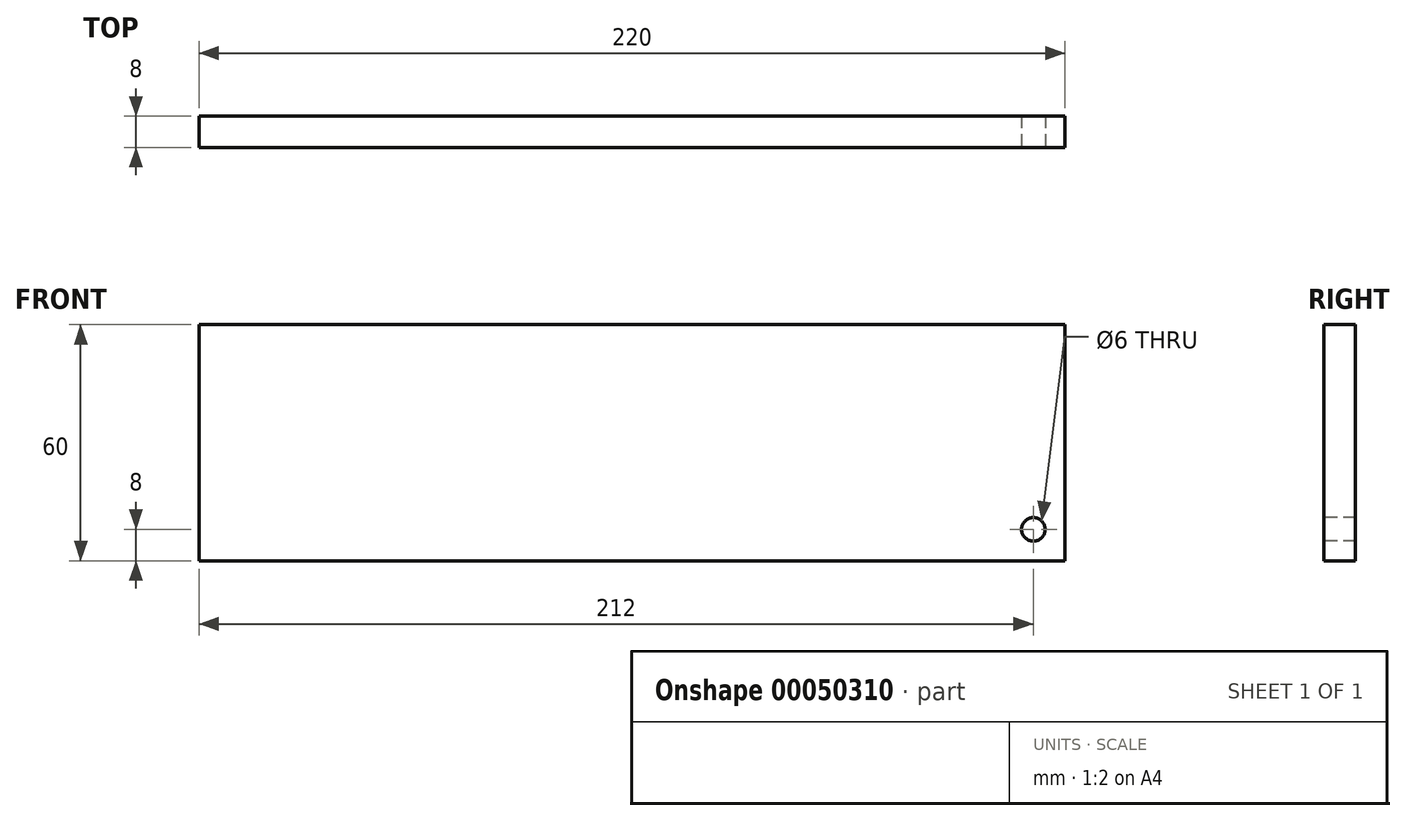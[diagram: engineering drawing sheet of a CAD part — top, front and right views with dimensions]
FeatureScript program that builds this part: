
annotation { "Feature Type Name" : "Feature", "Feature Type Description" : "" }
export const myFeature = defineFeature(function(context is Context, id is Id, definition is map)
    precondition{}
    {
        {
            var Q0;
            Q0=qCreatedBy(makeId("Front.planeOp"),FACE);
            var sketch = newSketch(context, id + "F0", { "sketchPlane" : qUnion([Q0])});
            skLineSegment(sketch, "E0.bottom", {"start": v(0, 0) * mm, "end": v(-220, 0) * mm});
            skLineSegment(sketch, "E0.top", {"start": v(0, -60) * mm, "end": v(-220, -60) * mm});
            skLineSegment(sketch, "E0.left", {"start": v(0, 0) * mm, "end": v(0, -60) * mm});
            skLineSegment(sketch, "E0.right", {"start": v(-220, 0) * mm, "end": v(-220, -60) * mm});
            skSolve(sketch);
        }
        {
            var Q0;
            Q0 = qSketchRegion(id + "F0", true);
            extrude(context, id + "F1", {"entities" : qUnion([Q0]), "depth" : 8 * mm});
        }
        {
            var Q0;
            Q0=makeQuery(id+"F1.opExtrude","CAP_FACE",FACE,{"disambiguationData":[OSD([sQuery(id+"F0.wireOp",EDGE,"E0.bottom"),sQuery(id+"F0.wireOp",EDGE,"E0.top"),sQuery(id+"F0.wireOp",EDGE,"E0.left"),sQuery(id+"F0.wireOp",EDGE,"E0.right")])],"isStart":false});
            var sketch = newSketch(context, id + "F2", { "sketchPlane" : qUnion([Q0])});
            skPoint(sketch, "E1", {"position": v(-220, 0) * mm});
            skPoint(sketch, "E2", {"position": v(-8, -52) * mm});
            skSolve(sketch);
        }
        {
            var Q0;
            Q0=sQuery(id+"F2.wireOp",VERTEX,"E2");
            var Q1;
            Q1=makeQuery(id+"F1.opExtrude","SWEPT_BODY",BODY,{"disambiguationData":[OSD([sQuery(id+"F0.wireOp",EDGE,"E0.bottom"),sQuery(id+"F0.wireOp",EDGE,"E0.top"),sQuery(id+"F0.wireOp",EDGE,"E0.left"),sQuery(id+"F0.wireOp",EDGE,"E0.right")])]});
            hole(context, id + "F3", {"style" : HoleStyle.SIMPLE, "holeDiameter" : 6 * mm, "endStyle" : HoleEndStyle.THROUGH, "locations" : qUnion([Q0]), "scope" : qUnion([Q1])});
        }
    });
